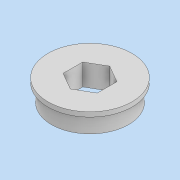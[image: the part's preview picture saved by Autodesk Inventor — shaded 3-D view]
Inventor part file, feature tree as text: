
AUTODESK INVENTOR PART (.ipt)
format: ipt  version: 2022 (Build 260153000, 153)  size: 108,032 bytes
history: native  units: in
note: dims shown in document units (in); Inventor stores cm internally (conversion verified against a paired STEP export)
features: extrude x2, sketch x2
ambient origin geometry x8: Origin, YZ Plane, XZ Plane, XY Plane, X Axis, Y Axis, Z Axis, Center Point
bodies: Solid1 (feature_tree)
feature tree (4):
  extrude  "Extrusion1"  Depth=0.2494in
  extrude  "Extrusion2"  Depth=0.0669in
  sketch  "Sketch1"  dims[d0=1.1268in d1=0.2494in]
  sketch  "Sketch2"  dims[d2=0.315in d3=0.0in d4=1.2272in d5=0.0669in d6=0.0in]
